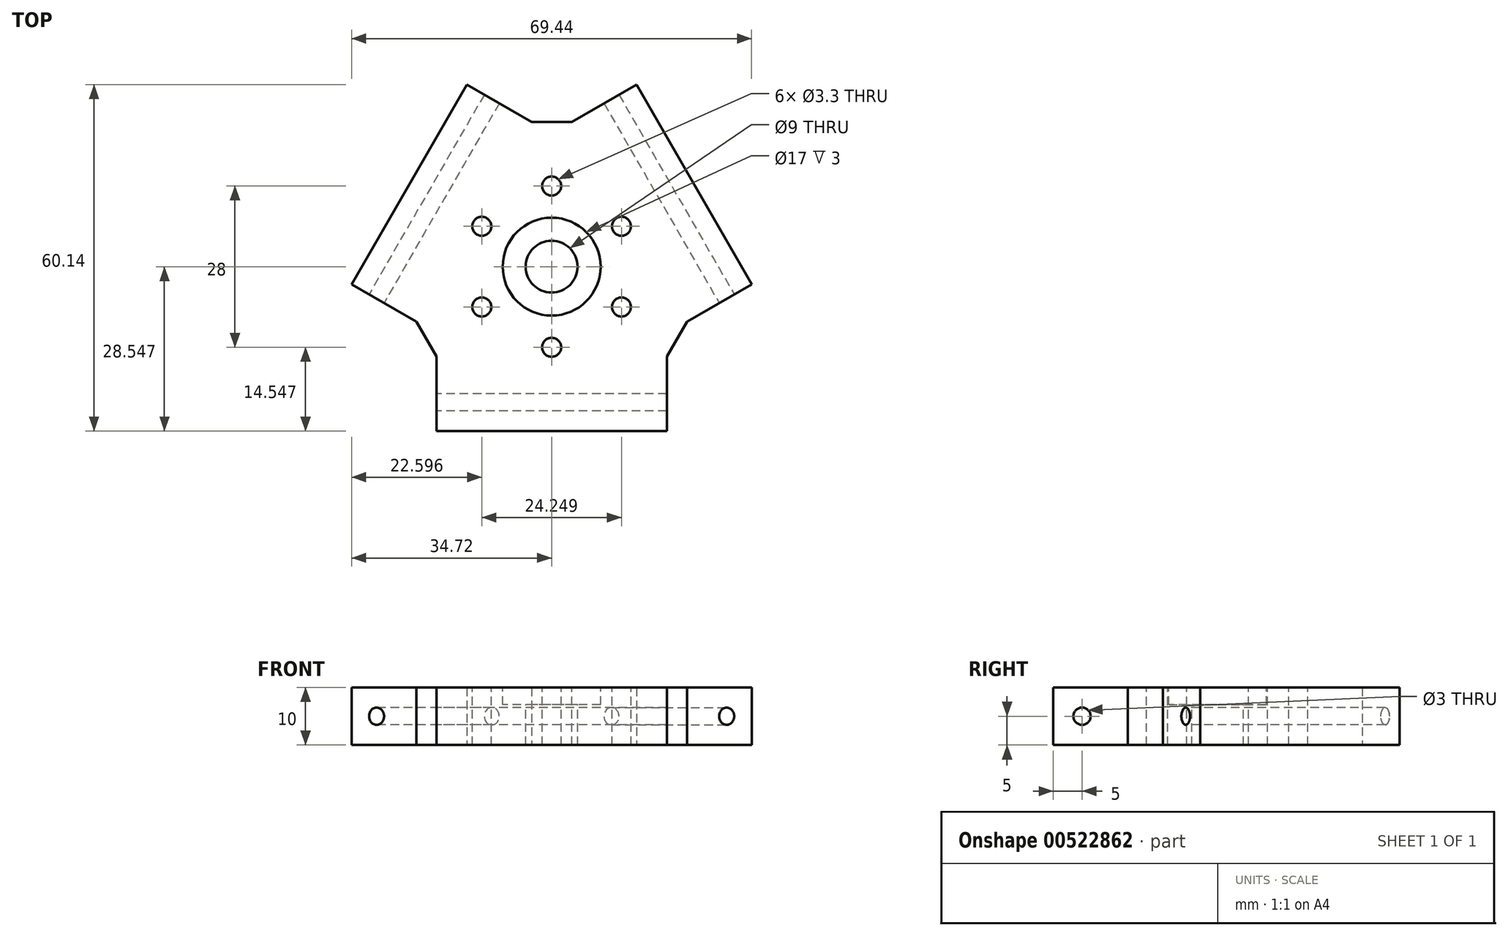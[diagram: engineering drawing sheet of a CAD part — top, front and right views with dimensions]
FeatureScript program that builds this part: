
annotation { "Feature Type Name" : "Feature", "Feature Type Description" : "" }
export const myFeature = defineFeature(function(context is Context, id is Id, definition is map)
    precondition{}
    {
        {
            var Q0;
            Q0=qCreatedBy(makeId("Top.planeOp"),FACE);
            var sketch = newSketch(context, id + "F0", { "sketchPlane" : qUnion([Q0])});
            skLineSegment(sketch, "E0", {"start": v(0, 0) * mm, "end": v(20, 34.64) * mm});
            skLineSegment(sketch, "E1", {"start": v(20, 34.64) * mm, "end": v(40, 0) * mm});
            skLineSegment(sketch, "E2", {"start": v(40, 0) * mm, "end": v(0, 0) * mm});
            skSolve(sketch);
        }
        {
            var Q0;
            Q0 = qSketchRegion(id + "F0", true);
            extrude(context, id + "F1", {"entities" : qUnion([Q0]), "depth" : 10 * mm, "offsetDistance" : 25 * mm});
        }
        {
            var Q0;
            Q0=makeQuery(id+"F1.opExtrude","SWEPT_FACE",FACE,{"disambiguationData":[OSD([sQuery(id+"F0.wireOp",EDGE,"E0")])]});
            extrude(context, id + "F2", {"entities" : qUnion([Q0]), "operationType" : NewBodyOperationType.ADD, "depth" : 17 * mm, "offsetDistance" : 25 * mm});
        }
        {
            var Q0;
            Q0=makeQuery(id+"F1.opExtrude","SWEPT_FACE",FACE,{"disambiguationData":[OSD([sQuery(id+"F0.wireOp",EDGE,"E1")])]});
            extrude(context, id + "F3", {"entities" : qUnion([Q0]), "operationType" : NewBodyOperationType.ADD, "depth" : 17 * mm, "offsetDistance" : 25 * mm});
        }
        {
            var Q0;
            Q0=makeQuery(id+"F1.opExtrude","SWEPT_FACE",FACE,{"disambiguationData":[OSD([sQuery(id+"F0.wireOp",EDGE,"E2")])]});
            extrude(context, id + "F4", {"entities" : qUnion([Q0]), "operationType" : NewBodyOperationType.ADD, "depth" : 17 * mm, "offsetDistance" : 25 * mm});
        }
        {
            var Q0;
            {var subQ0=sQuery(id+"F0.wireOp",EDGE,"E2");var subQ1=sQuery(id+"F0.wireOp",EDGE,"E1");var subQ2=sQuery(id+"F0.wireOp",EDGE,"E0");Q0=makeQuery(id+"F4.boolean.opBoolean","MERGE",FACE,{"derivedFrom":[makeQuery(id+"F3.boolean.opBoolean","MERGE",FACE,{"derivedFrom":[makeQuery(id+"F2.boolean.opBoolean","MERGE",FACE,{"derivedFrom":[makeQuery(id+"F1.opExtrude","CAP_FACE",FACE,{"disambiguationData":[OSD([subQ2,subQ1,subQ0])],"isStart":false}),makeQuery(id+"F2.opExtrude","SWEPT_FACE",FACE,{"disambiguationData":[OSD([subQ2]),TDD([makeQuery(id+"F1.opExtrude","CAP_EDGE",EDGE,{"disambiguationData":[OSD([subQ2])],"isStart":false})])]})]}),makeQuery(id+"F3.opExtrude","SWEPT_FACE",FACE,{"disambiguationData":[OSD([subQ1]),TDD([makeQuery(id+"F1.opExtrude","CAP_EDGE",EDGE,{"disambiguationData":[OSD([subQ1])],"isStart":false})])]})]}),makeQuery(id+"F4.opExtrude","SWEPT_FACE",FACE,{"disambiguationData":[OSD([subQ0]),TDD([makeQuery(id+"F1.opExtrude","CAP_EDGE",EDGE,{"disambiguationData":[OSD([subQ0])],"isStart":false})])]})]});}
            var sketch = newSketch(context, id + "F5", { "sketchPlane" : qUnion([Q0])});
            skLineSegment(sketch, "E3", {"start": v(20, 34.64) * mm, "end": v(20, 27.2) * mm});
            skLineSegment(sketch, "E4", {"start": v(40, 0) * mm, "end": v(33.55, 3.72) * mm});
            skLineSegment(sketch, "E5", {"start": v(0, 0) * mm, "end": v(6.45, 3.72) * mm});
            skCircle(sketch, "E6", {"center": v(20, 11.55) * mm, "radius": 4.5 * mm});
            skCircle(sketch, "E7", {"center": v(20, 11.55) * mm, "radius": 8.5 * mm});
            skCircle(sketch, "E8", {"center": v(20, 25.55) * mm, "radius": 1.65 * mm});
            skCircle(sketch, "E9.1.0", {"center": v(7.88, 18.55) * mm, "radius": 1.65 * mm});
            skCircle(sketch, "E9.2.0", {"center": v(7.88, 4.55) * mm, "radius": 1.65 * mm});
            skCircle(sketch, "E10.1.3.0", {"center": v(20, -2.45) * mm, "radius": 1.65 * mm});
            skCircle(sketch, "E10.1.4.0", {"center": v(32.12, 4.55) * mm, "radius": 1.65 * mm});
            skCircle(sketch, "E10.1.5.0", {"center": v(32.12, 18.55) * mm, "radius": 1.65 * mm});
            skLineSegment(sketch, "E11.trimOffspring", {"start": v(6.45, 19.37) * mm, "end": v(-4.72, 25.82) * mm});
            skLineSegment(sketch, "E12.trimOffspring", {"start": v(9.3, 5.37) * mm, "end": v(12.64, 7.3) * mm});
            skLineSegment(sketch, "E13.trimOffspring", {"start": v(20, -4.1) * mm, "end": v(20, -17) * mm});
            skLineSegment(sketch, "E14.trimOffspring", {"start": v(30.7, 5.37) * mm, "end": v(27.36, 7.3) * mm});
            skLineSegment(sketch, "E15.trimOffspring", {"start": v(12.64, 15.8) * mm, "end": v(9.3, 17.72) * mm});
            skLineSegment(sketch, "E16.trimOffspring", {"start": v(27.36, 15.8) * mm, "end": v(30.7, 17.72) * mm});
            skLineSegment(sketch, "E17.trimOffspring", {"start": v(20, 3.05) * mm, "end": v(20, -0.8) * mm});
            skLineSegment(sketch, "E18.trimOffspring", {"start": v(33.55, 19.37) * mm, "end": v(44.72, 25.82) * mm});
            skSolve(sketch);
        }
        {
            var Q0;
            {var subQ0=sQuery(id+"F5.wireOp",EDGE,"E9.1.0");var subQ1=makeQuery(id+"F5.imprint","INTERSECT",VERTEX,{"derivedFrom":[subQ0,sQuery(id+"F5.wireOp",EDGE,"E11.trimOffspring")]});Q0=makeQuery(id+"F5.imprint","IMPRINT",FACE,{"disambiguationData":[TD([[makeQuery(id+"F5.imprint","IMPRINT",EDGE,{"disambiguationData":[TD([[subQ1,-1.0]])],"derivedFrom":subQ0}),1.0]])]});}
            var Q1;
            Q1=makeQuery(id+"F5.imprint","IMPRINT",FACE,{"disambiguationData":[TD([[makeQuery(id+"F5.imprint","IMPRINT",EDGE,{"derivedFrom":sQuery(id+"F5.wireOp",EDGE,"E8")}),1.0]])]});
            var Q2;
            {var subQ0=sQuery(id+"F5.wireOp",EDGE,"E10.1.5.0");var subQ1=makeQuery(id+"F5.imprint","INTERSECT",VERTEX,{"derivedFrom":[subQ0,sQuery(id+"F5.wireOp",EDGE,"E16.trimOffspring")]});Q2=makeQuery(id+"F5.imprint","IMPRINT",FACE,{"disambiguationData":[TD([[makeQuery(id+"F5.imprint","IMPRINT",EDGE,{"disambiguationData":[TD([[subQ1,1.0]])],"derivedFrom":subQ0}),1.0]])]});}
            var Q3;
            {var subQ0=sQuery(id+"F5.wireOp",EDGE,"E10.1.4.0");var subQ1=makeQuery(id+"F5.imprint","INTERSECT",VERTEX,{"derivedFrom":[sQuery(id+"F5.wireOp",EDGE,"E4"),subQ0]});Q3=makeQuery(id+"F5.imprint","IMPRINT",FACE,{"disambiguationData":[TD([[makeQuery(id+"F5.imprint","IMPRINT",EDGE,{"disambiguationData":[TD([[subQ1,-1.0]])],"derivedFrom":subQ0}),1.0]])]});}
            var Q4;
            {var subQ0=sQuery(id+"F5.wireOp",EDGE,"E10.1.3.0");var subQ1=makeQuery(id+"F5.imprint","INTERSECT",VERTEX,{"derivedFrom":[subQ0,sQuery(id+"F5.wireOp",EDGE,"E13.trimOffspring")]});Q4=makeQuery(id+"F5.imprint","IMPRINT",FACE,{"disambiguationData":[TD([[makeQuery(id+"F5.imprint","IMPRINT",EDGE,{"disambiguationData":[TD([[subQ1,-1.0]])],"derivedFrom":subQ0}),1.0]])]});}
            var Q5;
            {var subQ0=sQuery(id+"F5.wireOp",EDGE,"E9.2.0");var subQ1=makeQuery(id+"F5.imprint","INTERSECT",VERTEX,{"derivedFrom":[sQuery(id+"F5.wireOp",EDGE,"E5"),subQ0]});Q5=makeQuery(id+"F5.imprint","IMPRINT",FACE,{"disambiguationData":[TD([[makeQuery(id+"F5.imprint","IMPRINT",EDGE,{"disambiguationData":[TD([[subQ1,-1.0]])],"derivedFrom":subQ0}),1.0]])]});}
            var Q6;
            Q6=makeQuery(id+"F5.imprint","IMPRINT",FACE,{"disambiguationData":[TD([[makeQuery(id+"F5.imprint","IMPRINT",EDGE,{"derivedFrom":sQuery(id+"F5.wireOp",EDGE,"E6")}),1.0]])]});
            extrude(context, id + "F6", {"entities" : qUnion([Q0, Q1, Q2, Q3, Q4, Q5, Q6]), "operationType" : NewBodyOperationType.REMOVE, "oppositeDirection" : true, "depth" : 25 * mm, "offsetDistance" : 25 * mm});
        }
        {
            var Q0;
            Q0=makeQuery(id+"F5.imprint","IMPRINT",FACE,{"disambiguationData":[TD([[makeQuery(id+"F5.imprint","IMPRINT",EDGE,{"derivedFrom":sQuery(id+"F5.wireOp",EDGE,"E6")}),-1.0]])]});
            extrude(context, id + "F7", {"entities" : qUnion([Q0]), "operationType" : NewBodyOperationType.REMOVE, "oppositeDirection" : true, "depth" : 3 * mm, "offsetDistance" : 25 * mm});
        }
        {
            var Q0;
            {var subQ0=sQuery(id+"F0.wireOp",EDGE,"E2");var subQ1=sQuery(id+"F0.wireOp",EDGE,"E0");Q0=makeQuery(id+"F4.boolean.opBoolean","MERGE",EDGE,{"derivedFrom":[makeQuery(id+"F2.boolean.opBoolean","MERGE",EDGE,{"derivedFrom":[makeQuery(id+"F1.opExtrude","SWEPT_EDGE",EDGE,{"disambiguationData":[OSD([subQ1,subQ0])]}),makeQuery(id+"F2.opExtrude","CAP_EDGE",EDGE,{"disambiguationData":[OSD([subQ1,subQ0])],"isStart":true})]}),makeQuery(id+"F4.opExtrude","CAP_EDGE",EDGE,{"disambiguationData":[OSD([subQ1,subQ0])],"isStart":true})]});}
            var Q1;
            {var subQ0=sQuery(id+"F0.wireOp",EDGE,"E2");var subQ1=sQuery(id+"F0.wireOp",EDGE,"E1");Q1=makeQuery(id+"F4.boolean.opBoolean","MERGE",EDGE,{"derivedFrom":[makeQuery(id+"F3.boolean.opBoolean","MERGE",EDGE,{"derivedFrom":[makeQuery(id+"F1.opExtrude","SWEPT_EDGE",EDGE,{"disambiguationData":[OSD([subQ1,subQ0])]}),makeQuery(id+"F3.opExtrude","CAP_EDGE",EDGE,{"disambiguationData":[OSD([subQ1,subQ0])],"isStart":true})]}),makeQuery(id+"F4.opExtrude","CAP_EDGE",EDGE,{"disambiguationData":[OSD([subQ1,subQ0])],"isStart":true})]});}
            var Q2;
            {var subQ0=sQuery(id+"F0.wireOp",EDGE,"E1");var subQ1=sQuery(id+"F0.wireOp",EDGE,"E0");Q2=makeQuery(id+"F3.boolean.opBoolean","MERGE",EDGE,{"derivedFrom":[makeQuery(id+"F2.boolean.opBoolean","MERGE",EDGE,{"derivedFrom":[makeQuery(id+"F1.opExtrude","SWEPT_EDGE",EDGE,{"disambiguationData":[OSD([subQ1,subQ0])]}),makeQuery(id+"F2.opExtrude","CAP_EDGE",EDGE,{"disambiguationData":[OSD([subQ1,subQ0])],"isStart":true})]}),makeQuery(id+"F3.opExtrude","CAP_EDGE",EDGE,{"disambiguationData":[OSD([subQ1,subQ0])],"isStart":true})]});}
            chamfer(context, id + "F8", {"entities" : qUnion([Q0, Q1, Q2]), "width" : 7 * mm, "tangentPropagation" : true});
        }
        {
            var Q0;
            Q0=makeQuery(id+"F2.opExtrude","SWEPT_FACE",FACE,{"disambiguationData":[OSD([sQuery(id+"F0.wireOp",EDGE,"E0"),sQuery(id+"F0.wireOp",EDGE,"E2")])]});
            var sketch = newSketch(context, id + "F9", { "sketchPlane" : qUnion([Q0])});
            skCircle(sketch, "E19", {"center": v(-12, 5) * mm, "radius": 1.5 * mm});
            skPoint(sketch, "E19.centerSnap0", {"position": v(-17, 5) * mm});
            skPoint(sketch, "E19.centerSnap1", {"position": v(-12, 10) * mm});
            skSolve(sketch);
        }
        {
            var Q0;
            Q0 = qSketchRegion(id + "F9", true);
            extrude(context, id + "F10", {"entities" : qUnion([Q0]), "operationType" : NewBodyOperationType.REMOVE, "oppositeDirection" : true, "depth" : 45.3 * mm, "offsetDistance" : 25 * mm});
        }
        {
            var Q0;
            Q0=makeQuery(id+"F4.opExtrude","SWEPT_FACE",FACE,{"disambiguationData":[OSD([sQuery(id+"F0.wireOp",EDGE,"E0"),sQuery(id+"F0.wireOp",EDGE,"E2")])]});
            var sketch = newSketch(context, id + "F11", { "sketchPlane" : qUnion([Q0])});
            skCircle(sketch, "E20", {"center": v(12, 5) * mm, "radius": 1.5 * mm});
            skPoint(sketch, "E20.centerSnap0", {"position": v(17, 5) * mm});
            skPoint(sketch, "E20.centerSnap1", {"position": v(12, 10) * mm});
            skSolve(sketch);
        }
        {
            var Q0;
            Q0 = qSketchRegion(id + "F11", true);
            extrude(context, id + "F12", {"entities" : qUnion([Q0]), "operationType" : NewBodyOperationType.REMOVE, "oppositeDirection" : true, "depth" : 40 * mm, "offsetDistance" : 25 * mm});
        }
        {
            var Q0;
            Q0=makeQuery(id+"F3.opExtrude","SWEPT_FACE",FACE,{"disambiguationData":[OSD([sQuery(id+"F0.wireOp",EDGE,"E1"),sQuery(id+"F0.wireOp",EDGE,"E2")])]});
            var sketch = newSketch(context, id + "F13", { "sketchPlane" : qUnion([Q0])});
            skCircle(sketch, "E21", {"center": v(46.64, 5) * mm, "radius": 1.5 * mm});
            skPoint(sketch, "E21.centerSnap0", {"position": v(51.64, 5) * mm});
            skPoint(sketch, "E21.centerSnap1", {"position": v(46.64, 10) * mm});
            skSolve(sketch);
        }
        {
            var Q0;
            Q0 = qSketchRegion(id + "F13", true);
            extrude(context, id + "F14", {"entities" : qUnion([Q0]), "operationType" : NewBodyOperationType.REMOVE, "oppositeDirection" : true, "depth" : 40 * mm, "offsetDistance" : 25 * mm});
        }
    });
